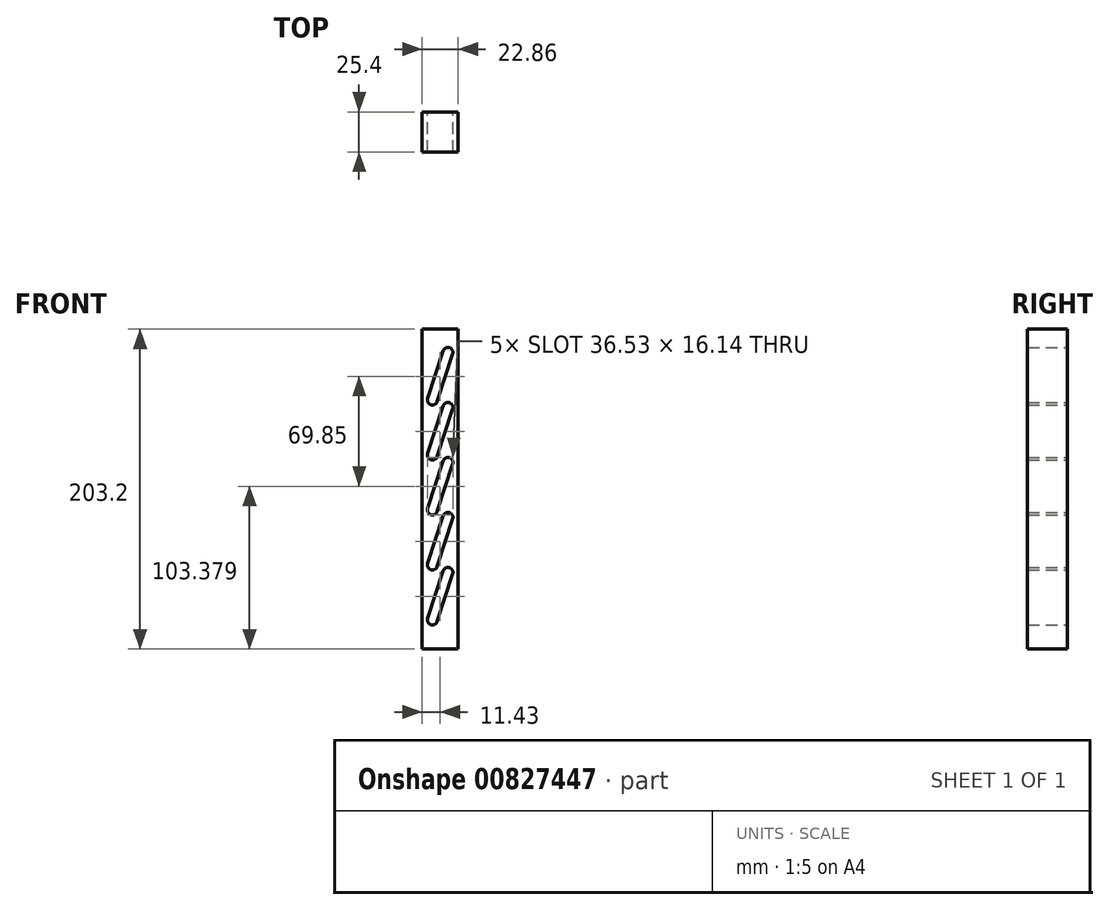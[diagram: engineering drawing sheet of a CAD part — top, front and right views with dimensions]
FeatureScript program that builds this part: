
annotation { "Feature Type Name" : "Feature", "Feature Type Description" : "" }
export const myFeature = defineFeature(function(context is Context, id is Id, definition is map)
    precondition{}
    {
        {
            var Q0;
            Q0=qCreatedBy(makeId("Front.planeOp"),FACE);
            var sketch = newSketch(context, id + "F0", { "sketchPlane" : qUnion([Q0])});
            skLineSegment(sketch, "E0.bottom", {"start": v(-11.77, 113.42) * mm, "end": v(11.1, 113.42) * mm});
            skLineSegment(sketch, "E0.top", {"start": v(-11.77, -89.78) * mm, "end": v(11.1, -89.78) * mm});
            skLineSegment(sketch, "E0.left", {"start": v(-11.77, 113.42) * mm, "end": v(-11.77, -89.78) * mm});
            skLineSegment(sketch, "E0.right", {"start": v(11.1, 113.42) * mm, "end": v(11.1, -89.78) * mm});
            skLineSegment(sketch, "E1", {"start": v(-2.23, 67.37) * mm, "end": v(7.58, 97.57) * mm});
            skLineSegment(sketch, "E2", {"start": v(-8.27, 69.33) * mm, "end": v(1.55, 99.53) * mm});
            skArc(sketch, "E3", {"start": v(7.58, 97.57) * mm, "mid": v(5.55, 101.57) * mm, "end": v(1.55, 99.53) * mm});
            skArc(sketch, "E4", {"start": v(-8.27, 69.33) * mm, "mid": v(-6.23, 65.33) * mm, "end": v(-2.23, 67.37) * mm});
            skLineSegment(sketch, "E5", {"start": v(-2.23, 32.45) * mm, "end": v(7.58, 62.64) * mm});
            skLineSegment(sketch, "E6", {"start": v(-8.26, 34.4) * mm, "end": v(1.55, 64.6) * mm});
            skArc(sketch, "E7", {"start": v(7.58, 62.64) * mm, "mid": v(5.55, 66.64) * mm, "end": v(1.55, 64.6) * mm});
            skArc(sketch, "E8", {"start": v(-8.26, 34.4) * mm, "mid": v(-6.23, 30.4) * mm, "end": v(-2.23, 32.45) * mm});
            skLineSegment(sketch, "E9", {"start": v(-2.23, -2.48) * mm, "end": v(7.58, 27.72) * mm});
            skLineSegment(sketch, "E10", {"start": v(-8.27, -0.52) * mm, "end": v(1.55, 29.68) * mm});
            skArc(sketch, "E11", {"start": v(7.58, 27.72) * mm, "mid": v(5.55, 31.72) * mm, "end": v(1.55, 29.68) * mm});
            skArc(sketch, "E12", {"start": v(-8.27, -0.52) * mm, "mid": v(-6.23, -4.52) * mm, "end": v(-2.23, -2.48) * mm});
            skLineSegment(sketch, "E13", {"start": v(-2.23, -37.4) * mm, "end": v(7.58, -7.2) * mm});
            skLineSegment(sketch, "E14", {"start": v(-8.27, -35.44) * mm, "end": v(1.55, -5.25) * mm});
            skArc(sketch, "E15", {"start": v(7.58, -7.2) * mm, "mid": v(5.55, -3.2) * mm, "end": v(1.55, -5.25) * mm});
            skArc(sketch, "E16", {"start": v(-8.27, -35.44) * mm, "mid": v(-6.23, -39.44) * mm, "end": v(-2.23, -37.4) * mm});
            skLineSegment(sketch, "E17", {"start": v(-2.23, -72.33) * mm, "end": v(7.58, -42.14) * mm});
            skLineSegment(sketch, "E18", {"start": v(-8.27, -70.37) * mm, "end": v(1.55, -40.17) * mm});
            skArc(sketch, "E19", {"start": v(7.58, -42.14) * mm, "mid": v(5.55, -38.13) * mm, "end": v(1.55, -40.17) * mm});
            skArc(sketch, "E20", {"start": v(-8.27, -70.37) * mm, "mid": v(-6.23, -74.37) * mm, "end": v(-2.23, -72.33) * mm});
            skSolve(sketch);
        }
        {
            var Q0;
            Q0=makeQuery(id+"F0.imprint","IMPRINT",FACE,{"disambiguationData":[TD([[makeQuery(id+"F0.imprint","IMPRINT",EDGE,{"derivedFrom":sQuery(id+"F0.wireOp",EDGE,"E0.bottom")}),-1.0]])]});
            extrude(context, id + "F1", {"entities" : qUnion([Q0]), "depth" : 25.4 * mm, "offsetDistance" : 25.4 * mm});
        }
    });
